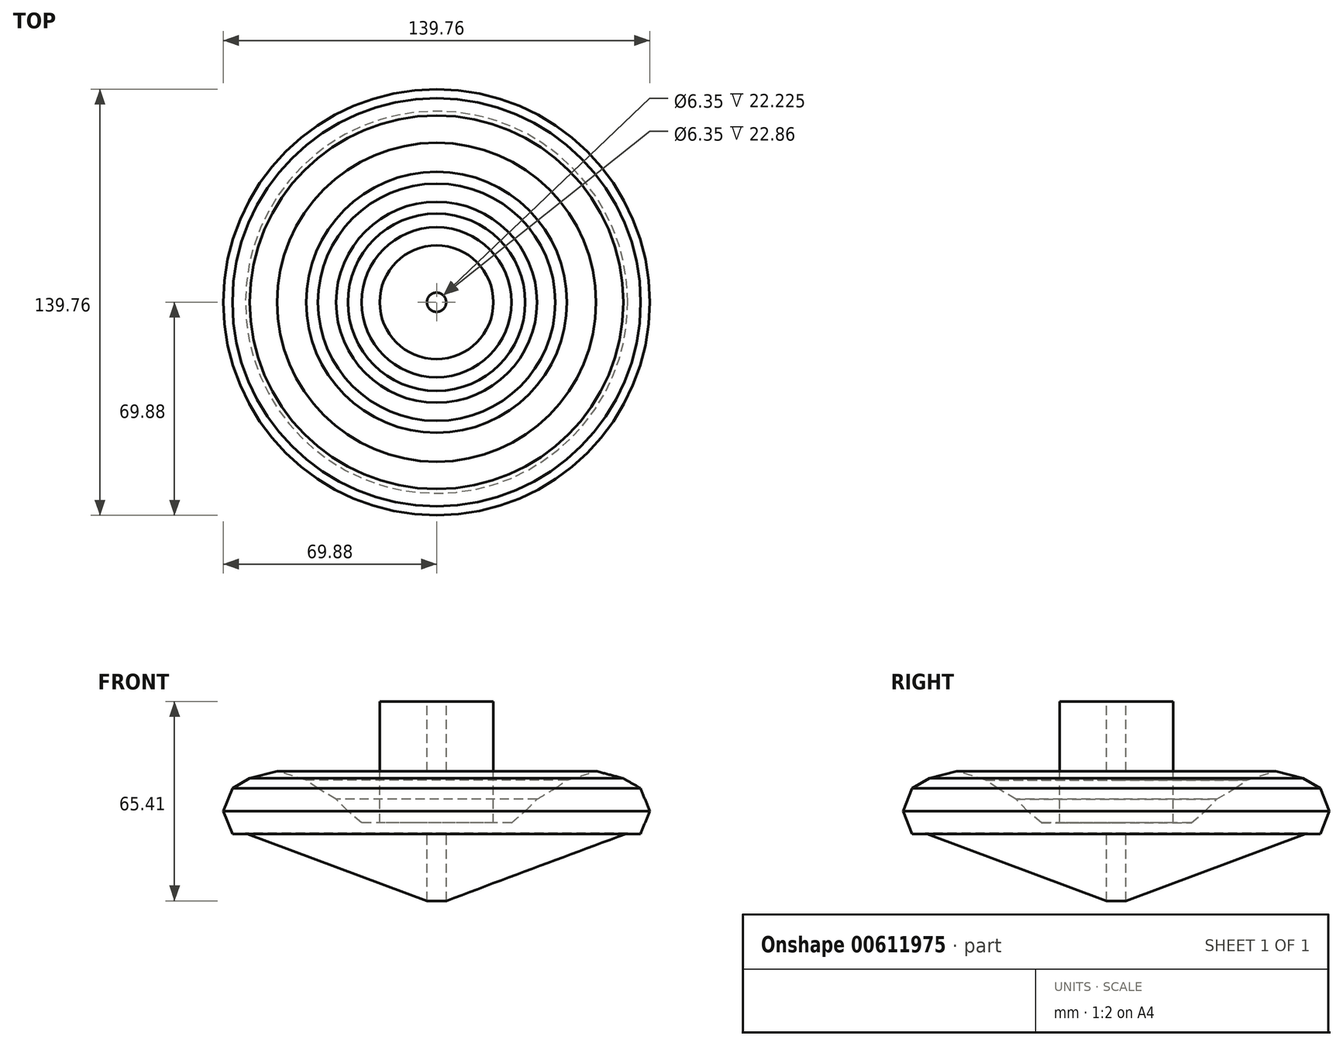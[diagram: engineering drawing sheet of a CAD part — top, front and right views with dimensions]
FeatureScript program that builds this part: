
annotation { "Feature Type Name" : "Feature", "Feature Type Description" : "" }
export const myFeature = defineFeature(function(context is Context, id is Id, definition is map)
    precondition{}
    {
        {
            var Q0;
            Q0=qCreatedBy(makeId("Front.planeOp"),FACE);
            var sketch = newSketch(context, id + "F0", { "sketchPlane" : qUnion([Q0])});
            skLineSegment(sketch, "E0", {"start": v(0, 22.23) * mm, "end": v(3.17, 22.23) * mm});
            skLineSegment(sketch, "E1", {"start": v(3.17, 22.23) * mm, "end": v(3.18, 0) * mm});
            skLineSegment(sketch, "E2", {"start": v(3.17, 0) * mm, "end": v(62.66, 22.23) * mm});
            skLineSegment(sketch, "E3", {"start": v(62.66, 22.23) * mm, "end": v(66.9, 21.98) * mm});
            skLineSegment(sketch, "E4", {"start": v(66.9, 21.98) * mm, "end": v(69.88, 29.43) * mm});
            skLineSegment(sketch, "E5", {"start": v(69.88, 29.43) * mm, "end": v(66.9, 36.88) * mm});
            skLineSegment(sketch, "E6", {"start": v(66.9, 36.88) * mm, "end": v(61.24, 40.16) * mm});
            skLineSegment(sketch, "E7", {"start": v(61.24, 40.16) * mm, "end": v(52.3, 42.55) * mm});
            skLineSegment(sketch, "E8", {"start": v(52.3, 42.55) * mm, "end": v(42.76, 39.57) * mm});
            skLineSegment(sketch, "E9", {"start": v(42.76, 39.57) * mm, "end": v(38.89, 36.88) * mm});
            skLineSegment(sketch, "E10", {"start": v(38.89, 36.88) * mm, "end": v(32.93, 33.3) * mm});
            skLineSegment(sketch, "E11", {"start": v(32.93, 33.3) * mm, "end": v(29.05, 29.43) * mm});
            skLineSegment(sketch, "E12", {"start": v(29.05, 29.43) * mm, "end": v(24.58, 25.56) * mm});
            skLineSegment(sketch, "E13", {"start": v(24.58, 25.56) * mm, "end": v(18.62, 25.56) * mm});
            skLineSegment(sketch, "E14", {"start": v(18.62, 36.88) * mm, "end": v(18.62, 25.56) * mm});
            skLineSegment(sketch, "E15", {"start": v(18.62, 36.88) * mm, "end": v(18.62, 48.5) * mm});
            skLineSegment(sketch, "E16", {"start": v(18.62, 48.5) * mm, "end": v(18.62, 65.4) * mm});
            skLineSegment(sketch, "E17", {"start": v(18.62, 65.4) * mm, "end": v(3.17, 65.4) * mm});
            skLineSegment(sketch, "E18", {"start": v(3.17, 65.4) * mm, "end": v(3.17, 42.55) * mm});
            skLineSegment(sketch, "E19", {"start": v(3.17, 42.55) * mm, "end": v(0, 42.55) * mm});
            skLineSegment(sketch, "E20", {"start": v(0, 42.55) * mm, "end": v(0, 22.23) * mm});
            skSolve(sketch);
        }
        {
            var Q0;
            Q0=makeQuery(id+"F0.imprint","IMPRINT",FACE,{"disambiguationData":[TD([[makeQuery(id+"F0.imprint","IMPRINT",EDGE,{"derivedFrom":sQuery(id+"F0.wireOp",EDGE,"E0")}),1.0]])]});
            var Q1;
            Q1=sQuery(id+"F0.wireOp",EDGE,"E20");
            revolve(context, id + "F1", {"entities" : qUnion([Q0]), "axis" : qUnion([Q1]), "revolveType" : RevolveType.FULL});
        }
    });
